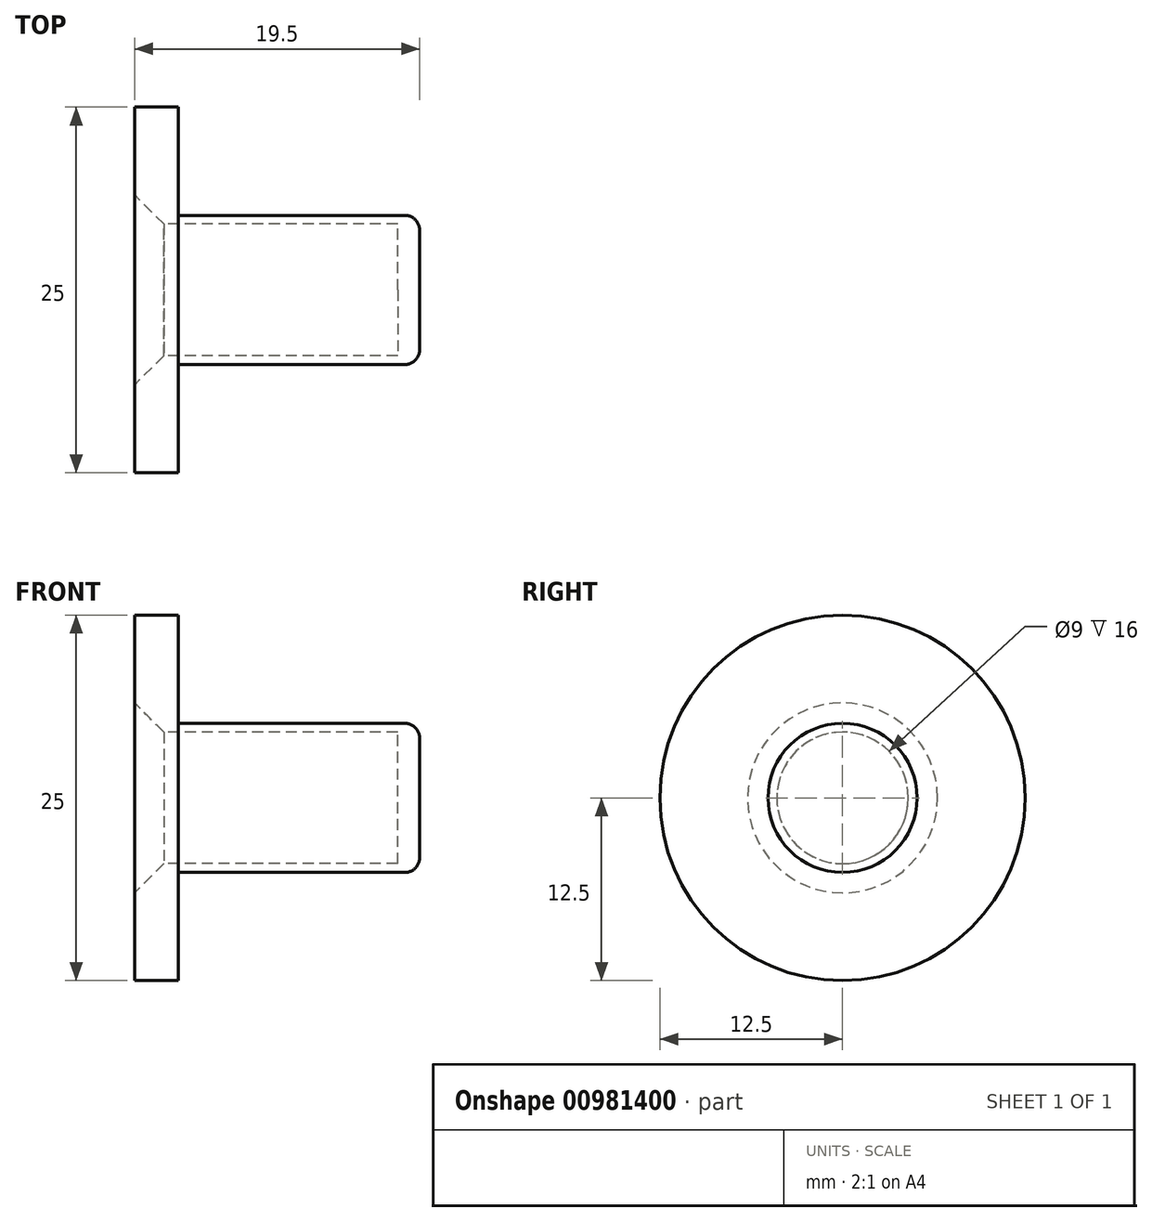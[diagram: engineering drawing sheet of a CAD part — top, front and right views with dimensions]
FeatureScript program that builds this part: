
annotation { "Feature Type Name" : "Feature", "Feature Type Description" : "" }
export const myFeature = defineFeature(function(context is Context, id is Id, definition is map)
    precondition{}
    {
        {
            var Q0;
            Q0=qCreatedBy(makeId("Right.planeOp"),FACE);
            var sketch = newSketch(context, id + "F0", { "sketchPlane" : qUnion([Q0])});
            skCircle(sketch, "E0", {"center": v(0, 0) * mm, "radius": 4.5 * mm});
            skCircle(sketch, "E1", {"center": v(0, 0) * mm, "radius": 5.1 * mm});
            skSolve(sketch);
        }
        {
            var Q0;
            Q0 = qSketchRegion(id + "F0", true);
            extrude(context, id + "F1", {"entities" : qUnion([Q0]), "depth" : 15 * mm, "offsetDistance" : 25 * mm});
        }
        {
            var Q0;
            Q0=makeQuery(id+"F1.opExtrude","CAP_FACE",FACE,{"disambiguationData":[OSD([sQuery(id+"F0.wireOp",EDGE,"E0"),sQuery(id+"F0.wireOp",EDGE,"E1")])],"isStart":false});
            var sketch = newSketch(context, id + "F2", { "sketchPlane" : qUnion([Q0])});
            skCircle(sketch, "E2", {"center": v(0, 0) * mm, "radius": 5.1 * mm});
            skSolve(sketch);
        }
        {
            var Q0;
            Q0 = qSketchRegion(id + "F2", true);
            extrude(context, id + "F3", {"entities" : qUnion([Q0]), "operationType" : NewBodyOperationType.ADD, "depth" : 1.5 * mm, "offsetDistance" : 25 * mm});
        }
        {
            var Q0;
            Q0=makeQuery(id+"F1.opExtrude","CAP_FACE",FACE,{"disambiguationData":[OSD([sQuery(id+"F0.wireOp",EDGE,"E0"),sQuery(id+"F0.wireOp",EDGE,"E1")])],"isStart":true});
            var sketch = newSketch(context, id + "F4", { "sketchPlane" : qUnion([Q0])});
            skCircle(sketch, "E3", {"center": v(0, 0) * mm, "radius": 4.5 * mm});
            skCircle(sketch, "E4", {"center": v(0, 0) * mm, "radius": 12.5 * mm});
            skSolve(sketch);
        }
        {
            var Q0;
            Q0 = qSketchRegion(id + "F4", true);
            extrude(context, id + "F5", {"entities" : qUnion([Q0]), "operationType" : NewBodyOperationType.ADD, "depth" : 3 * mm, "offsetDistance" : 25 * mm});
        }
        {
            var Q0;
            Q0=makeQuery(id+"F3.opExtrude","CAP_EDGE",EDGE,{"disambiguationData":[OSD([sQuery(id+"F2.wireOp",EDGE,"E2")])],"isStart":false});
            var Q1;
            Q1=makeQuery(id+"F1.opExtrude","CAP_EDGE",EDGE,{"disambiguationData":[OSD([sQuery(id+"F0.wireOp",EDGE,"E1")])],"isStart":true});
            fillet(context, id + "F6", {"entities" : qUnion([Q0, Q1]), "radius" : 1 * mm, "tangentPropagation" : true, "allowEdgeOverflow" : false});
        }
        {
            var Q0;
            Q0=makeQuery(id+"F5.opExtrude","CAP_EDGE",EDGE,{"disambiguationData":[OSD([sQuery(id+"F4.wireOp",EDGE,"E3")])],"isStart":false});
            chamfer(context, id + "F7", {"entities" : qUnion([Q0]), "width" : 2 * mm, "tangentPropagation" : true});
        }
    });
